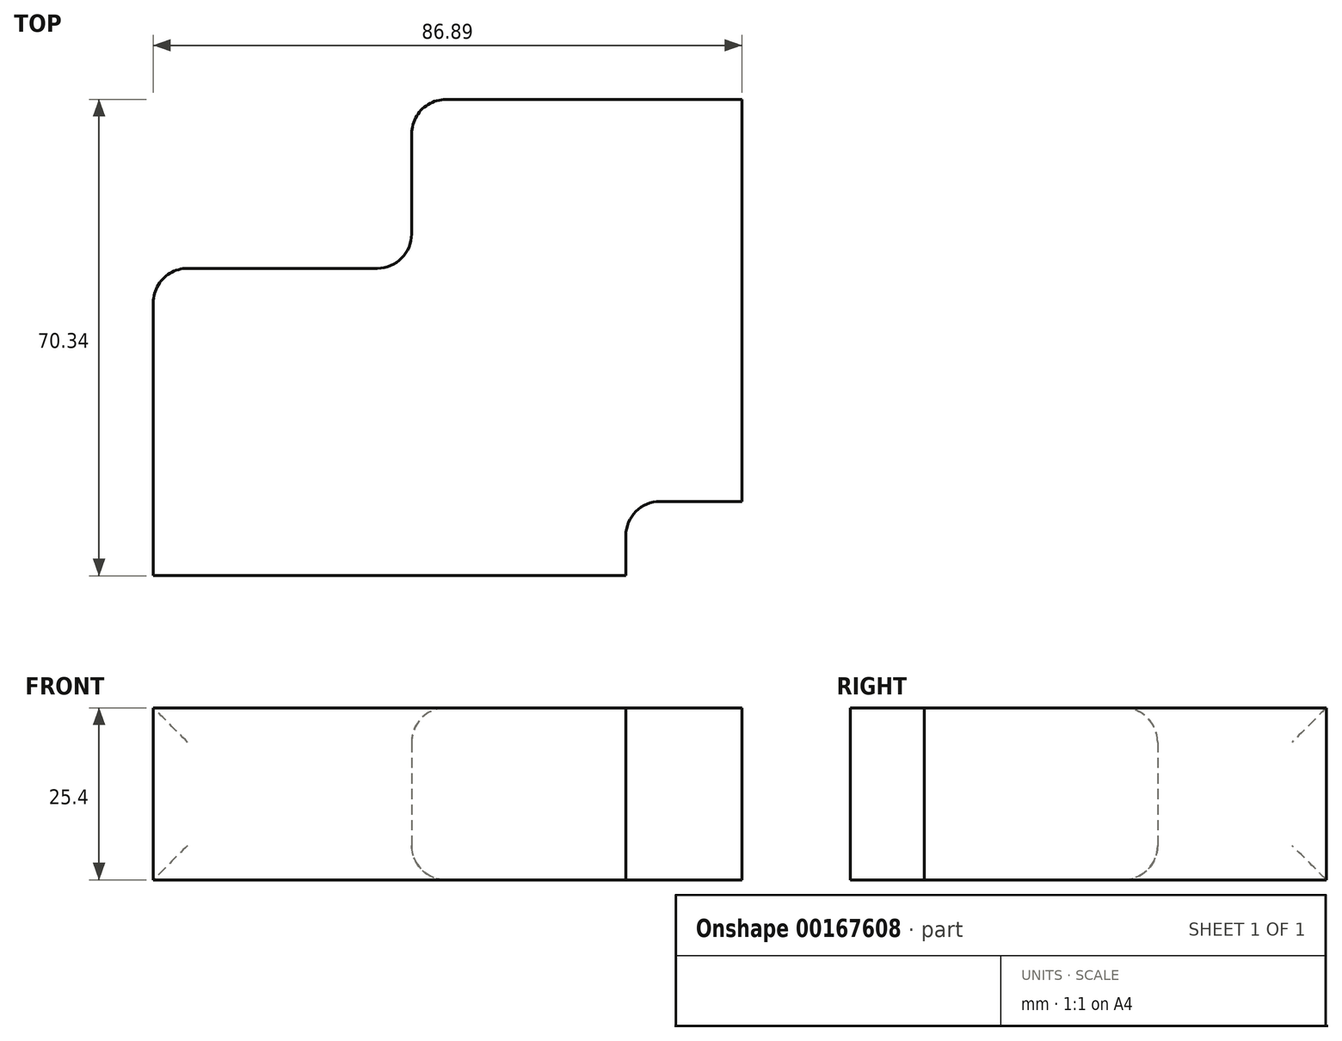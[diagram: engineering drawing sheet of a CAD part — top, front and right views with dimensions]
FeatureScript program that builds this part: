
annotation { "Feature Type Name" : "Feature", "Feature Type Description" : "" }
export const myFeature = defineFeature(function(context is Context, id is Id, definition is map)
    precondition{}
    {
        {
            var Q0;
            Q0=qCreatedBy(makeId("Top.planeOp"),FACE);
            var sketch = newSketch(context, id + "F0", { "sketchPlane" : qUnion([Q0])});
            skLineSegment(sketch, "E0.bottom", {"start": v(-30.8, 16.37) * mm, "end": v(38.98, 16.37) * mm});
            skLineSegment(sketch, "E0.top", {"start": v(-30.8, -29.03) * mm, "end": v(38.98, -29.03) * mm});
            skLineSegment(sketch, "E0.left", {"start": v(-30.8, 16.37) * mm, "end": v(-30.8, -29.03) * mm});
            skLineSegment(sketch, "E0.right", {"start": v(38.98, 16.37) * mm, "end": v(38.98, -29.03) * mm});
            skLineSegment(sketch, "E1.bottom", {"start": v(7.35, 41.3) * mm, "end": v(56.1, 41.3) * mm});
            skLineSegment(sketch, "E1.top", {"start": v(7.35, -18.05) * mm, "end": v(56.1, -18.05) * mm});
            skLineSegment(sketch, "E1.left", {"start": v(7.35, 41.3) * mm, "end": v(7.35, -18.05) * mm});
            skLineSegment(sketch, "E1.right", {"start": v(56.1, 41.3) * mm, "end": v(56.1, -18.05) * mm});
            skSolve(sketch);
        }
        {
            var Q0;
            Q0 = qSketchRegion(id + "F0", true);
            extrude(context, id + "F1", {"entities" : qUnion([Q0]), "depth" : 25.4 * mm});
        }
        {
            var Q0;
            Q0=makeQuery(id+"F1.opExtrude","SWEPT_FACE",FACE,{"disambiguationData":[OSD([sQuery(id+"F0.wireOp",EDGE,"E0.bottom")])]});
            var Q1;
            Q1=makeQuery(id+"F1.opExtrude","SWEPT_FACE",FACE,{"disambiguationData":[OSD([sQuery(id+"F0.wireOp",EDGE,"E1.left")])]});
            var Q2;
            Q2=makeQuery(id+"F1.opExtrude","SWEPT_EDGE",EDGE,{"disambiguationData":[OSD([sQuery(id+"F0.wireOp",EDGE,"E0.bottom"),sQuery(id+"F0.wireOp",EDGE,"E1.left")])]});
            var Q3;
            Q3=makeQuery(id+"F1.opExtrude","CAP_EDGE",EDGE,{"disambiguationData":[OSD([sQuery(id+"F0.wireOp",EDGE,"E0.bottom")])],"isStart":false});
            var Q4;
            Q4=makeQuery(id+"F1.opExtrude","CAP_EDGE",EDGE,{"disambiguationData":[OSD([sQuery(id+"F0.wireOp",EDGE,"E1.left")])],"isStart":false});
            var Q5;
            Q5=makeQuery(id+"F1.opExtrude","SWEPT_EDGE",EDGE,{"disambiguationData":[OSD([sQuery(id+"F0.wireOp",EDGE,"E0.right"),sQuery(id+"F0.wireOp",EDGE,"E1.top")])]});
            fillet(context, id + "F2", {"entities" : qUnion([Q0, Q1, Q2, Q3, Q4, Q5]), "radius" : 5.08 * mm, "tangentPropagation" : true, "allowEdgeOverflow" : false});
        }
    });
